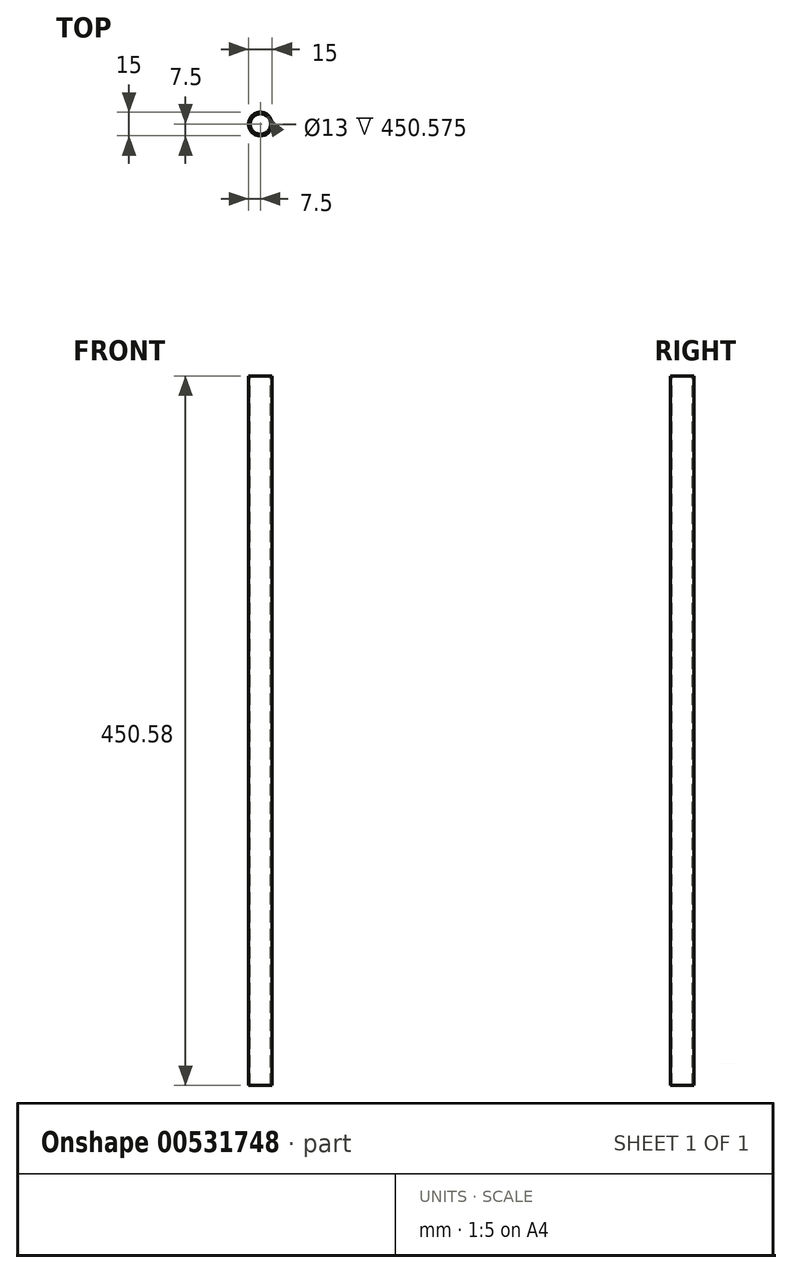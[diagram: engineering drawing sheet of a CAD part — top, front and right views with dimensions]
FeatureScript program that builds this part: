
annotation { "Feature Type Name" : "Feature", "Feature Type Description" : "" }
export const myFeature = defineFeature(function(context is Context, id is Id, definition is map)
    precondition{}
    {
        {
            var Q0;
            Q0=qCreatedBy(makeId("Front.planeOp"),FACE);
            var sketch = newSketch(context, id + "F0", { "sketchPlane" : qUnion([Q0])});
            skLineSegment(sketch, "E0", {"start": v(-7.5, 63.23) * mm, "end": v(-7.5, -386.77) * mm});
            skLineSegment(sketch, "E1", {"start": v(-7.5, -386.77) * mm, "end": v(-1, -386.77) * mm});
            skLineSegment(sketch, "E2", {"start": v(-1, -386.77) * mm, "end": v(0, -386.77) * mm});
            skLineSegment(sketch, "E3", {"start": v(0, -386.77) * mm, "end": v(0, 63.8) * mm});
            skLineSegment(sketch, "E4", {"start": v(0, 63.8) * mm, "end": v(-1, 63.8) * mm});
            skLineSegment(sketch, "E5", {"start": v(-1, 63.8) * mm, "end": v(-7.5, 63.23) * mm});
            skLineSegment(sketch, "E6", {"start": v(-1, 63.8) * mm, "end": v(-1, -386.77) * mm});
            skSolve(sketch);
        }
        {
            var Q0;
            Q0=makeQuery(id+"F0.imprint","IMPRINT",FACE,{"disambiguationData":[TD([[makeQuery(id+"F0.imprint","IMPRINT",EDGE,{"derivedFrom":sQuery(id+"F0.wireOp",EDGE,"E2")}),1.0]])]});
            var Q1;
            Q1=sQuery(id+"F0.wireOp",EDGE,"E0");
            revolve(context, id + "F1", {"surfaceOperationType" : NewSurfaceOperationType.NEW, "entities" : qUnion([Q0]), "axis" : qUnion([Q1]), "revolveType" : RevolveType.FULL});
        }
    });
